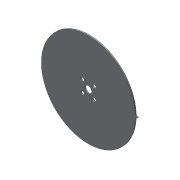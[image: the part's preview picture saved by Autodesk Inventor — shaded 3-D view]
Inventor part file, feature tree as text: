
AUTODESK INVENTOR PART (.ipt)
format: ipt  version: 2018 (Build 220112000, 112)  size: 115,712 bytes
history: native  units: mm
features: sketch x4, extrude x3, hole x1, fillet x1, projected_geometry x1
ambient origin geometry x8: Origin, YZ Plane, XZ Plane, XY Plane, X Axis, Y Axis, Z Axis, Center Point
bodies: Solid1 (feature_tree)
feature tree (10):
  extrude  "Extrusion1"  Depth=1.0mm
  extrude  "Extrusion2"  Depth=1.0mm TaperAngle=0.0deg
  hole  "Hole1"  [1 undecoded]
  extrude  "Extrusion3"  Depth=1.0mm
  fillet  "Fillet1"  Radius=1.0mm
  sketch  "Sketch1"  dims[d0=1.0mm d1=0.0mm d2=80.0mm]
  sketch  "Sketch2"  dims[d3=6.0mm d4=1.0mm d5=0.0mm]
  sketch  "Sketch3"  dims[d6=14.0mm d7=14.0mm]
  sketch  "Sketch4"  dims[d8=9.899495mm d9=9.899495mm d10=3.2mm d11=6.35mm d12=6.3mm d13=2.0mm d14=90.0deg d15=9.525mm d16=20.594885mm d18=1.0mm d19=1.0mm d20=42.0mm d21=1.0mm d22=0.0mm d23=1.0mm]
  projected_geometry  "Projected Loop1"
note: 1 required parameter value undecoded (feature->parameter linkage not recoverable at this tier; creation-order binding heuristic only, values carry confidence <= 0.55)
